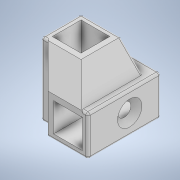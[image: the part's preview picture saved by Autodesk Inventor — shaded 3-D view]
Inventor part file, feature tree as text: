
AUTODESK INVENTOR PART (.ipt)
format: ipt  version: 2020.4 (Build 244396000, 396)  size: 189,952 bytes
history: native  units: in
note: dims shown in document units (in); Inventor stores cm internally (conversion verified against a paired STEP export)
features: extrude x5, sketch x5, chamfer x4, fillet x1
ambient origin geometry x8: Origin, YZ Plane, XZ Plane, XY Plane, X Axis, Y Axis, Z Axis, Center Point
bodies: Solid1 (feature_tree)
feature tree (15):
  extrude  "Extrusion1"  Depth=1.4173in
  extrude  "Extrusion2"  Depth=2.5906in
  extrude  "Extrusion3"  Depth=1.0236in TaperAngle=0.0deg
  extrude  "Extrusion4"  Depth=1.0236in
  chamfer  "Chamfer1"  Distance=2.3937in
  chamfer  "Chamfer2"  Distance=1.0236in
  extrude  "Extrusion5"  Depth=2.3937in TaperAngle=0.0deg
  chamfer  "Chamfer3"  Distance=0.7795in Angle=45.0deg
  chamfer  "Chamfer4"  Distance=0.7795in Angle=45.0deg
  fillet  "Fillet1"  Radius=0.4724in
  sketch  "Sketch1"  dims[d0=1.4173in d1=1.4173in]
  sketch  "Sketch2"  dims[d2=2.5906in d3=0.0in d4=2.5906in]
  sketch  "Sketch3"  dims[d5=1.4173in d6=1.0236in d7=0.3937in d8=0.0in d9=0.0in]
  sketch  "Sketch4"  dims[d10=1.0236in d11=1.0236in d12=2.3937in d13=0.0in]
  sketch  "Sketch5"  dims[d14=1.0236in d15=1.0236in d16=2.3937in d17=0.0in d18=0.7795in d19=0.0787in d20=45.0deg d21=0.7795in d22=0.0787in d23=45.0deg d24=0.4724in d25=2.7559in d26=0.0in d27=0.1969in d28=0.0787in d29=45.0deg d30=0.1969in d31=0.0787in d32=45.0deg d33=0.0787in]
